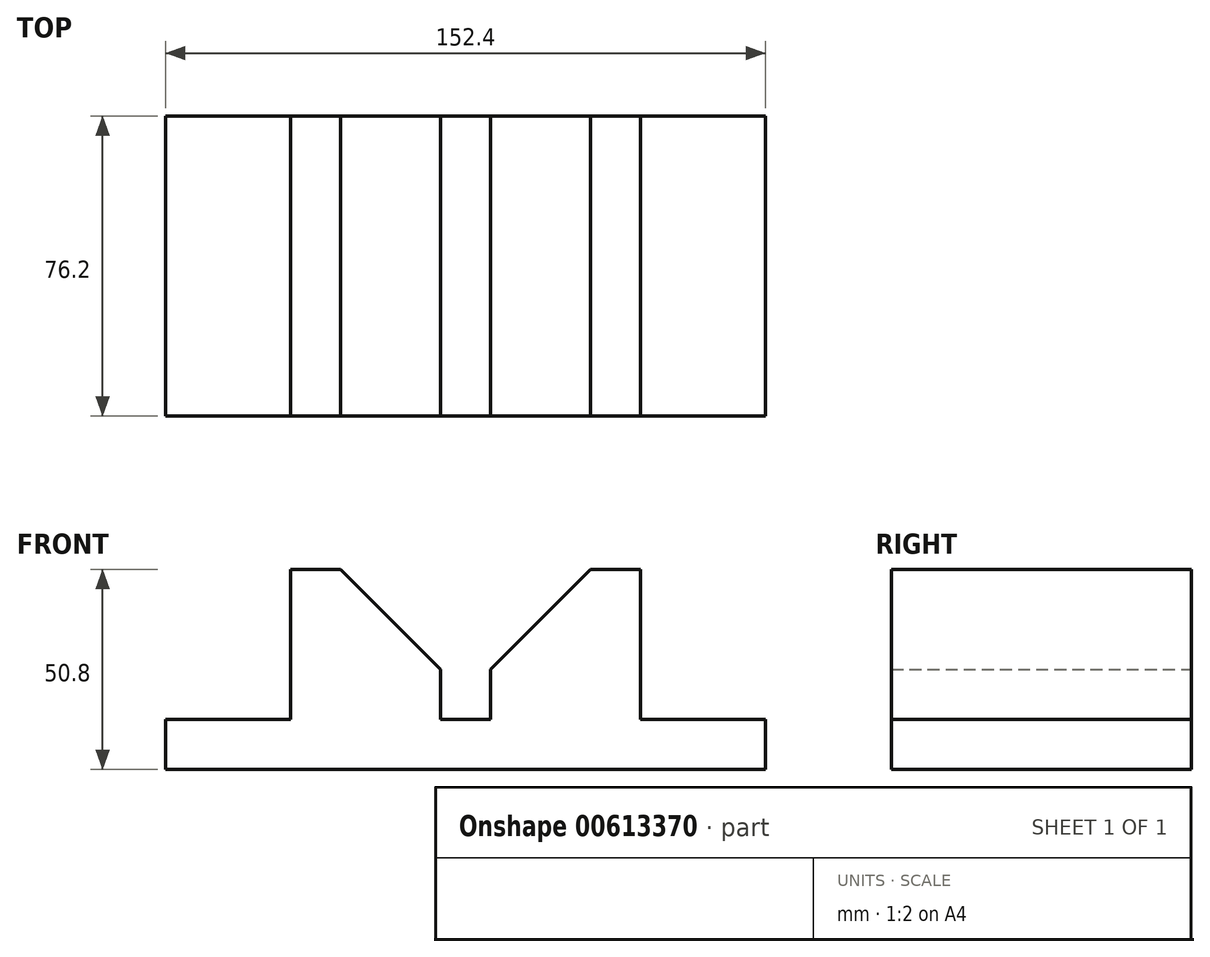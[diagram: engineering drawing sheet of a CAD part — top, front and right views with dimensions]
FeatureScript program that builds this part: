
annotation { "Feature Type Name" : "Feature", "Feature Type Description" : "" }
export const myFeature = defineFeature(function(context is Context, id is Id, definition is map)
    precondition{}
    {
        {
            var Q0;
            Q0=qCreatedBy(makeId("Front.planeOp"),FACE);
            var sketch = newSketch(context, id + "F0", { "sketchPlane" : qUnion([Q0])});
            skLineSegment(sketch, "E0", {"start": v(0, 0) * mm, "end": v(152.4, 0) * mm});
            skLineSegment(sketch, "E1", {"start": v(152.4, 0) * mm, "end": v(152.4, 12.7) * mm});
            skLineSegment(sketch, "E2", {"start": v(152.4, 12.7) * mm, "end": v(120.65, 12.7) * mm});
            skLineSegment(sketch, "E3", {"start": v(120.65, 12.7) * mm, "end": v(120.65, 50.8) * mm});
            skLineSegment(sketch, "E4", {"start": v(120.65, 50.8) * mm, "end": v(107.95, 50.8) * mm});
            skLineSegment(sketch, "E5", {"start": v(107.95, 50.8) * mm, "end": v(82.56, 25.4) * mm});
            skLineSegment(sketch, "E6", {"start": v(82.56, 25.4) * mm, "end": v(82.56, 12.7) * mm});
            skLineSegment(sketch, "E7", {"start": v(82.56, 12.7) * mm, "end": v(69.86, 12.7) * mm});
            skLineSegment(sketch, "E8", {"start": v(69.86, 12.7) * mm, "end": v(69.86, 25.4) * mm});
            skLineSegment(sketch, "E9", {"start": v(69.86, 25.4) * mm, "end": v(44.47, 50.8) * mm});
            skLineSegment(sketch, "E10", {"start": v(44.47, 50.8) * mm, "end": v(31.75, 50.8) * mm});
            skLineSegment(sketch, "E11", {"start": v(31.75, 50.8) * mm, "end": v(31.75, 12.7) * mm});
            skLineSegment(sketch, "E12", {"start": v(31.75, 12.7) * mm, "end": v(0, 12.7) * mm});
            skLineSegment(sketch, "E13", {"start": v(0, 12.7) * mm, "end": v(0, 0) * mm});
            skSolve(sketch);
        }
        {
            var Q0;
            Q0=makeQuery(id+"F0.imprint","IMPRINT",FACE,{"disambiguationData":[TD([[makeQuery(id+"F0.imprint","IMPRINT",EDGE,{"derivedFrom":sQuery(id+"F0.wireOp",EDGE,"E0")}),1.0]])]});
            extrude(context, id + "F1", {"entities" : qUnion([Q0]), "depth" : 76.2 * mm, "offsetDistance" : 25.4 * mm});
        }
    });
